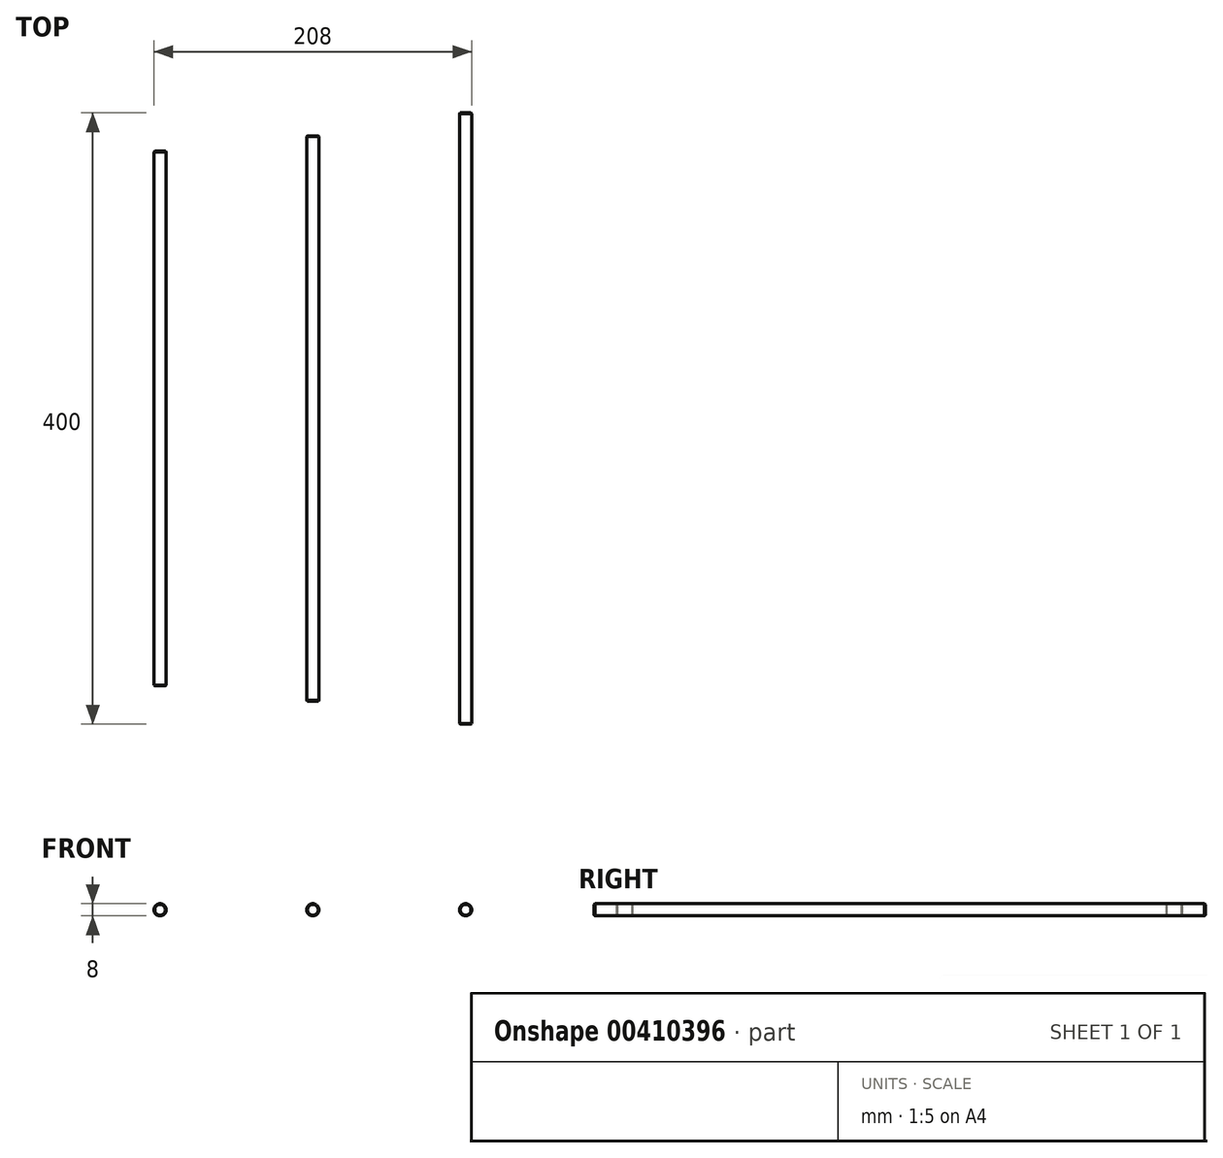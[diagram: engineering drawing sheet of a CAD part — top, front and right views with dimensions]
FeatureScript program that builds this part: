
annotation { "Feature Type Name" : "Feature", "Feature Type Description" : "" }
export const myFeature = defineFeature(function(context is Context, id is Id, definition is map)
    precondition{}
    {
        {
            var Q0;
            Q0=qCreatedBy(makeId("Front.planeOp"),FACE);
            var sketch = newSketch(context, id + "F0", { "sketchPlane" : qUnion([Q0])});
            skCircle(sketch, "E0", {"center": v(0, 0) * mm, "radius": 4 * mm});
            skSolve(sketch);
        }
        {
            var Q0;
            Q0=makeQuery(id+"F0.imprint","IMPRINT",FACE,{"disambiguationData":[TD([[makeQuery(id+"F0.imprint","IMPRINT",EDGE,{"derivedFrom":sQuery(id+"F0.wireOp",EDGE,"E0")}),1.0]])]});
            extrude(context, id + "F1", {"entities" : qUnion([Q0]), "endBound" : BoundingType.SYMMETRIC, "depth" : 400 * mm});
        }
        {
            var Q0;
            Q0=makeQuery(id+"F1.opExtrude","CAP_EDGE",EDGE,{"disambiguationData":[OSD([sQuery(id+"F0.wireOp",EDGE,"E0")])],"isStart":false});
            var Q1;
            Q1=makeQuery(id+"F1.opExtrude","CAP_EDGE",EDGE,{"disambiguationData":[OSD([sQuery(id+"F0.wireOp",EDGE,"E0")])],"isStart":true});
            chamfer(context, id + "F2", {"entities" : qUnion([Q0, Q1]), "width" : .5 * mm, "tangentPropagation" : true});
        }
        {
            var Q0;
            Q0=makeQuery(id+"F1.opExtrude","SWEPT_BODY",BODY,{"disambiguationData":[OSD([sQuery(id+"F0.wireOp",EDGE,"E0")])]});
            transform(context, id + "F3", {"entities" : qUnion([Q0]), "transformType" : TransformType.TRANSLATION_3D, "dx" : 200 * mm, "dy" : 0 * mm, "dz" : 0 * mm, "makeCopy" : false});
        }
        {
            var Q0;
            Q0=makeQuery(id+"F0.imprint","IMPRINT",FACE,{"disambiguationData":[TD([[makeQuery(id+"F0.imprint","IMPRINT",EDGE,{"derivedFrom":sQuery(id+"F0.wireOp",EDGE,"E0")}),1.0]])]});
            extrude(context, id + "F4", {"entities" : qUnion([Q0]), "endBound" : BoundingType.SYMMETRIC, "depth" : 370 * mm});
        }
        {
            var Q0;
            Q0=makeQuery(id+"F4.opExtrude","CAP_EDGE",EDGE,{"disambiguationData":[OSD([sQuery(id+"F0.wireOp",EDGE,"E0")])],"isStart":false});
            var Q1;
            Q1=makeQuery(id+"F4.opExtrude","CAP_EDGE",EDGE,{"disambiguationData":[OSD([sQuery(id+"F0.wireOp",EDGE,"E0")])],"isStart":true});
            chamfer(context, id + "F5", {"entities" : qUnion([Q0, Q1]), "width" : .5 * mm, "tangentPropagation" : true});
        }
        {
            var Q0;
            Q0=makeQuery(id+"F4.opExtrude","SWEPT_BODY",BODY,{"disambiguationData":[OSD([sQuery(id+"F0.wireOp",EDGE,"E0")])]});
            transform(context, id + "F6", {"entities" : qUnion([Q0]), "transformType" : TransformType.TRANSLATION_3D, "dx" : 100 * mm, "dy" : 0 * mm, "dz" : 0 * mm, "makeCopy" : false});
        }
        {
            var Q0;
            Q0=makeQuery(id+"F0.imprint","IMPRINT",FACE,{"disambiguationData":[TD([[makeQuery(id+"F0.imprint","IMPRINT",EDGE,{"derivedFrom":sQuery(id+"F0.wireOp",EDGE,"E0")}),1.0]])]});
            extrude(context, id + "F7", {"entities" : qUnion([Q0]), "endBound" : BoundingType.SYMMETRIC, "depth" : 350 * mm});
        }
        {
            var Q0;
            Q0=makeQuery(id+"F7.opExtrude","CAP_EDGE",EDGE,{"disambiguationData":[OSD([sQuery(id+"F0.wireOp",EDGE,"E0")])],"isStart":false});
            var Q1;
            Q1=makeQuery(id+"F7.opExtrude","CAP_EDGE",EDGE,{"disambiguationData":[OSD([sQuery(id+"F0.wireOp",EDGE,"E0")])],"isStart":true});
            chamfer(context, id + "F8", {"entities" : qUnion([Q0, Q1]), "width" : .5 * mm, "tangentPropagation" : true});
        }
    });
